FCSTD DOCUMENT  (FreeCAD 0.16R6704 (Git))
Label: center
License: All rights reserved
LicenseURL: http://en.wikipedia.org/wiki/All_rights_reserved
objects: Sketcher::SketchObject×1
note: 1 computed .brp shape members not serialized (recipe doc carries the construction recipe); baked Part::Feature solids carry a one-line shape summary decoded from their .brp

FEATURE [Sketcher::SketchObject] Sketch
  sketch-geometry (8):
    g0: LineSegment StartX=6 StartY=0 StartZ=0 EndX=9 EndY=5.19615 EndZ=0
    g1: LineSegment StartX=9 StartY=5.19615 StartZ=0 EndX=6 EndY=10.3923 EndZ=0
    g2: LineSegment StartX=6 StartY=10.3923 StartZ=0 EndX=0 EndY=10.3923 EndZ=0
    g3: LineSegment StartX=0 StartY=10.3923 StartZ=0 EndX=-3 EndY=5.19615 EndZ=0
    g4: LineSegment StartX=-3 StartY=5.19615 StartZ=0 EndX=0 EndY=0 EndZ=0
    g5: LineSegment StartX=0 StartY=0 StartZ=0 EndX=6 EndY=0 EndZ=0
    g6: Circle [constr] CenterX=3 CenterY=5.19615 CenterZ=0 NormalX=0 NormalY=0 NormalZ=1 Radius=6
    g7: Circle CenterX=3 CenterY=5.19615 CenterZ=0 NormalX=0 NormalY=0 NormalZ=1 Radius=4
  constraints (20):
    c: Coincident(g0,g1)
    c: Coincident(g1,g2)
    c: Coincident(g2,g3)
    c: Coincident(g3,g4)
    c: Coincident(g4,g5)
    c: Coincident(g5,g0)
    c: Equal(g0, g1-g5) x5
    c: PointOnObject(g5,g-1)
    c: Horizontal(g5)
    c: DistanceX(g2,g2) = 6
    c: Radius(g6) = 6
    c: Coincident(g4,g-1)
    c: PointOnObject(g-1,g6)
    c: PointOnObject(g3,g6)
    c: PointOnObject(g2,g6)
    c: PointOnObject(g1,g6)
    c: PointOnObject(g0,g6)
    c: PointOnObject(g0,g6)
    c: Coincident(g7,g6)
    c: Radius(g7) = 4
